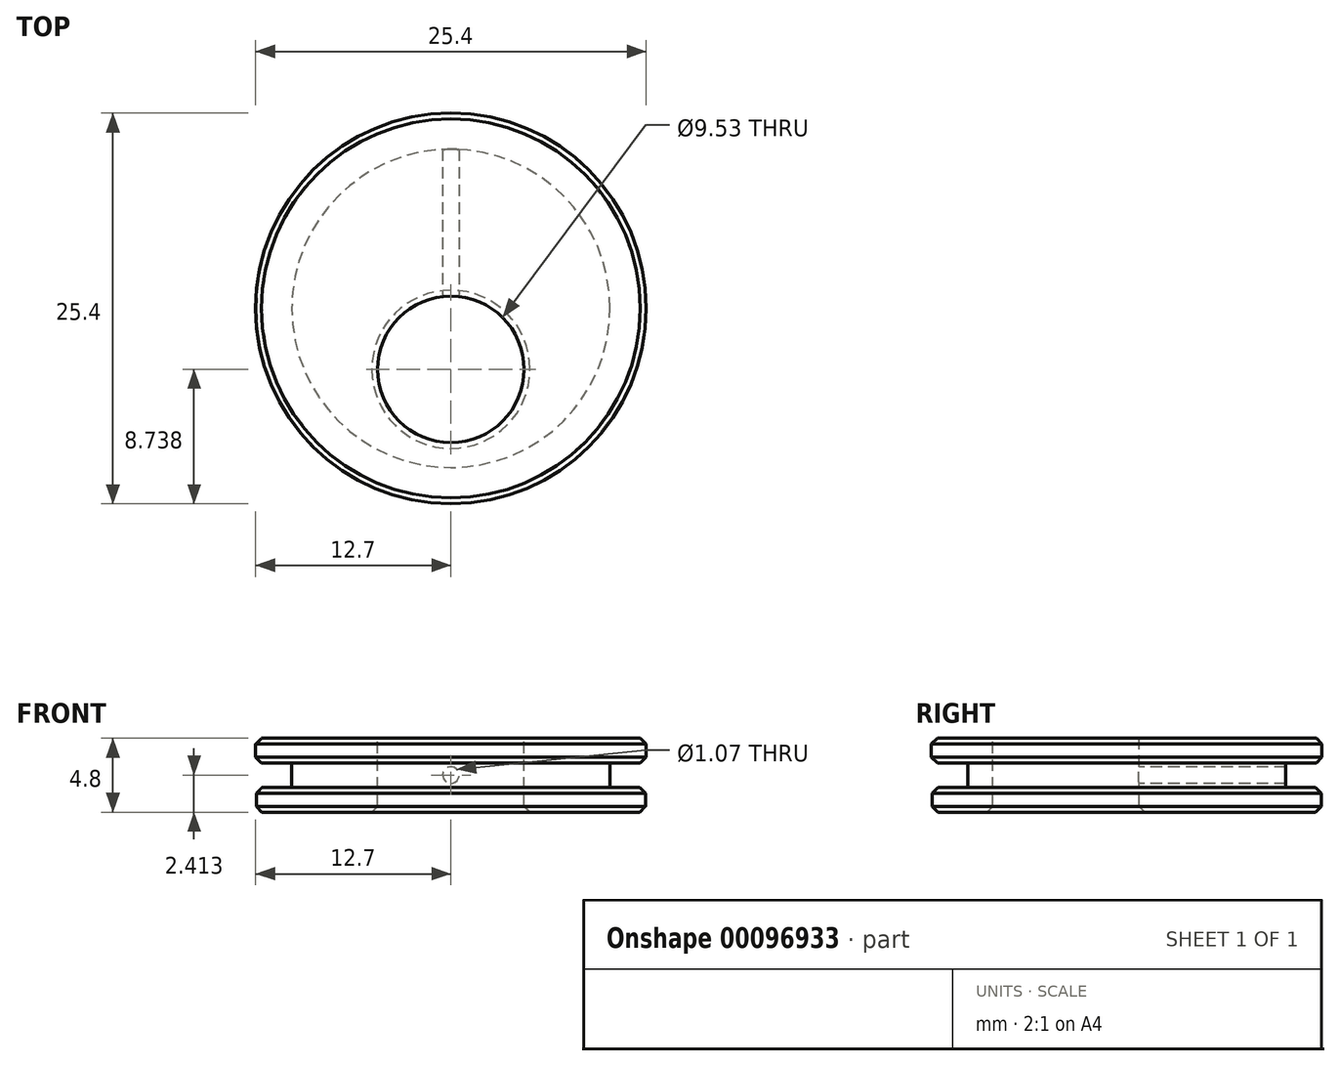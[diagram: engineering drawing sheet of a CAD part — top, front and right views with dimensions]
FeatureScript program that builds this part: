
annotation { "Feature Type Name" : "Feature", "Feature Type Description" : "" }
export const myFeature = defineFeature(function(context is Context, id is Id, definition is map)
    precondition{}
    {
        {
            var Q0;
            Q0=qCreatedBy(makeId("Front.planeOp"),FACE);
            var sketch = newSketch(context, id + "F0", { "sketchPlane" : qUnion([Q0])});
            skLineSegment(sketch, "E0", {"start": v(0, 0) * mm, "end": v(0, 1.6) * mm});
            skLineSegment(sketch, "E1", {"start": v(0, 1.6) * mm, "end": v(12.7, 1.6) * mm});
            skLineSegment(sketch, "E2", {"start": v(12.7, 1.6) * mm, "end": v(12.7, 0) * mm});
            skLineSegment(sketch, "E3", {"start": v(12.7, 0) * mm, "end": v(10.35, 0) * mm});
            skLineSegment(sketch, "E4", {"start": v(10.35, 0) * mm, "end": v(10.35, -1.6) * mm});
            skLineSegment(sketch, "E5", {"start": v(10.35, -1.6) * mm, "end": v(12.66, -1.6) * mm});
            skLineSegment(sketch, "E6", {"start": v(12.66, -1.6) * mm, "end": v(12.66, -3.2) * mm});
            skLineSegment(sketch, "E7", {"start": v(12.66, -3.2) * mm, "end": v(0, -3.2) * mm});
            skLineSegment(sketch, "E8", {"start": v(0, -3.2) * mm, "end": v(0, 0) * mm});
            skSolve(sketch);
        }
        {
            var Q0;
            Q0=makeQuery(id+"F0.imprint","IMPRINT",FACE,{"disambiguationData":[TD([[makeQuery(id+"F0.imprint","IMPRINT",EDGE,{"derivedFrom":sQuery(id+"F0.wireOp",EDGE,"E0")}),-1.0]])]});
            var Q1;
            Q1=sQuery(id+"F0.wireOp",EDGE,"E0");
            revolve(context, id + "F1", {"entities" : qUnion([Q0]), "axis" : qUnion([Q1]), "revolveType" : RevolveType.FULL});
        }
        {
            var Q0;
            Q0=makeQuery(id+"F1.opRevolve","SWEPT_FACE",FACE,{"disambiguationData":[OSD([sQuery(id+"F0.wireOp",EDGE,"E1")])]});
            var sketch = newSketch(context, id + "F2", { "sketchPlane" : qUnion([Q0])});
            skCircle(sketch, "E9", {"center": v(0, -3.96) * mm, "radius": 4.76 * mm});
            skSolve(sketch);
        }
        {
            var Q0;
            Q0=makeQuery(id+"F2.imprint","IMPRINT",FACE,{"disambiguationData":[TD([[makeQuery(id+"F2.imprint","IMPRINT",EDGE,{"derivedFrom":sQuery(id+"F2.wireOp",EDGE,"E9")}),1.0]])]});
            extrude(context, id + "F3", {"entities" : qUnion([Q0]), "operationType" : NewBodyOperationType.REMOVE, "oppositeDirection" : true, "depth" : 5.08 * mm});
        }
        {
            var Q0;
            Q0=makeQuery(id+"F3.boolean.opBoolean","COPY",EDGE,{"derivedFrom":makeQuery(id+"F3.opExtrude","CAP_EDGE",EDGE,{"disambiguationData":[OSD([sQuery(id+"F2.wireOp",EDGE,"E9")])],"isStart":true})});
            var Q1;
            Q1=makeQuery(id+"F1.opRevolve","SWEPT_EDGE",EDGE,{"disambiguationData":[OSD([sQuery(id+"F0.wireOp",EDGE,"E1"),sQuery(id+"F0.wireOp",EDGE,"E2")])]});
            var Q2;
            Q2=makeQuery(id+"F1.opRevolve","SWEPT_EDGE",EDGE,{"disambiguationData":[OSD([sQuery(id+"F0.wireOp",EDGE,"E2"),sQuery(id+"F0.wireOp",EDGE,"E3")])]});
            var Q3;
            Q3=makeQuery(id+"F1.opRevolve","SWEPT_EDGE",EDGE,{"disambiguationData":[OSD([sQuery(id+"F0.wireOp",EDGE,"E5"),sQuery(id+"F0.wireOp",EDGE,"E6")])]});
            var Q4;
            Q4=makeQuery(id+"F1.opRevolve","SWEPT_EDGE",EDGE,{"disambiguationData":[OSD([sQuery(id+"F0.wireOp",EDGE,"E6"),sQuery(id+"F0.wireOp",EDGE,"E7")])]});
            var Q5;
            Q5=makeQuery(id+"F3.boolean.opBoolean","INTERSECT",EDGE,{"derivedFrom":[makeQuery(id+"F1.opRevolve","SWEPT_FACE",FACE,{"disambiguationData":[OSD([sQuery(id+"F0.wireOp",EDGE,"E7")])]}),makeQuery(id+"F3.opExtrude","SWEPT_FACE",FACE,{"disambiguationData":[OSD([sQuery(id+"F2.wireOp",EDGE,"E9")])]})]});
            chamfer(context, id + "F4", {"entities" : qUnion([Q0, Q1, Q2, Q3, Q4, Q5]), "width" : 0.38 * mm, "tangentPropagation" : true});
        }
        {
            var Q0;
            Q0=qCreatedBy(makeId("Front.planeOp"),FACE);
            var sketch = newSketch(context, id + "F5", { "sketchPlane" : qUnion([Q0])});
            skCircle(sketch, "E10", {"center": v(0, -0.79) * mm, "radius": 0.53 * mm});
            skSolve(sketch);
        }
        {
            var Q0;
            Q0 = qSketchRegion(id + "F5", true);
            extrude(context, id + "F6", {"entities" : qUnion([Q0]), "operationType" : NewBodyOperationType.REMOVE, "oppositeDirection" : true, "depth" : 25.4 * mm});
        }
    });
